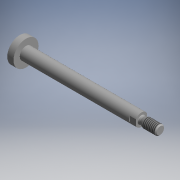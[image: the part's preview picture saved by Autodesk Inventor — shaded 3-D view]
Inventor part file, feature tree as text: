
AUTODESK INVENTOR PART (.ipt)
format: ipt  version: 2017.3 (Build 213256000, 256)  size: 140,288 bytes
history: native  units: mm (DEFAULTED — no unit token found)
features: other x21, sketch x4, revolve x3, thread x1, extrude x1
ambient origin geometry x8: Origin, YZ Plane, XZ Plane, XY Plane, X Axis, Y Axis, Z Axis, Center Point
bodies: Solid1 (feature_tree)
feature tree (30):
  revolve  "Revolution1"  Angle=360.0deg
  revolve  "Revolution2"  [1 undecoded]
  revolve  "Revolution3"  [1 undecoded]
  thread  "Thread1"  [1 undecoded]
  extrude  "Extrusion1"  [1 undecoded]
  other  "FDT_PIRODACC_M1_XY"
  other  "FDT_PIRODACC_M1_YZ"
  other  "FDT_PIRODACC_M1_ZX"
  other  "FDT_PIRODACC_M1_X"
  other  "FDT_PIRODACC_M1_Y"
  other  "FDT_PIRODACC_M1_Z"
  other  "FDT_PIRODACC_M1_Center"
  other  "NUT1_XY"
  other  "NUT1_YZ"
  other  "NUT1_ZX"
  other  "NUT1_X"
  other  "NUT1_Y"
  other  "NUT1_Z"
  other  "NUT1_Center"
  other  "PISTON_XY"
  other  "PISTON_YZ"
  other  "PISTON_ZX"
  other  "PISTON_X"
  other  "PISTON_Y"
  other  "PISTON_Z"
  other  "PISTON_Center"
  sketch  "Sketch_1"  dims[d0=360.0deg d1=360.0deg]
  sketch  "Sketch_11"  dims[d2=360.0deg d3=8.02589mm d4=0.0mm]
  sketch  "Sketch_19"  dims[d5=16.0mm d6=0.0mm d7=0.0mm]
  sketch  "Sketch_20"
note: 4 required parameter values undecoded (feature->parameter linkage not recoverable at this tier; creation-order binding heuristic only, values carry confidence <= 0.55)